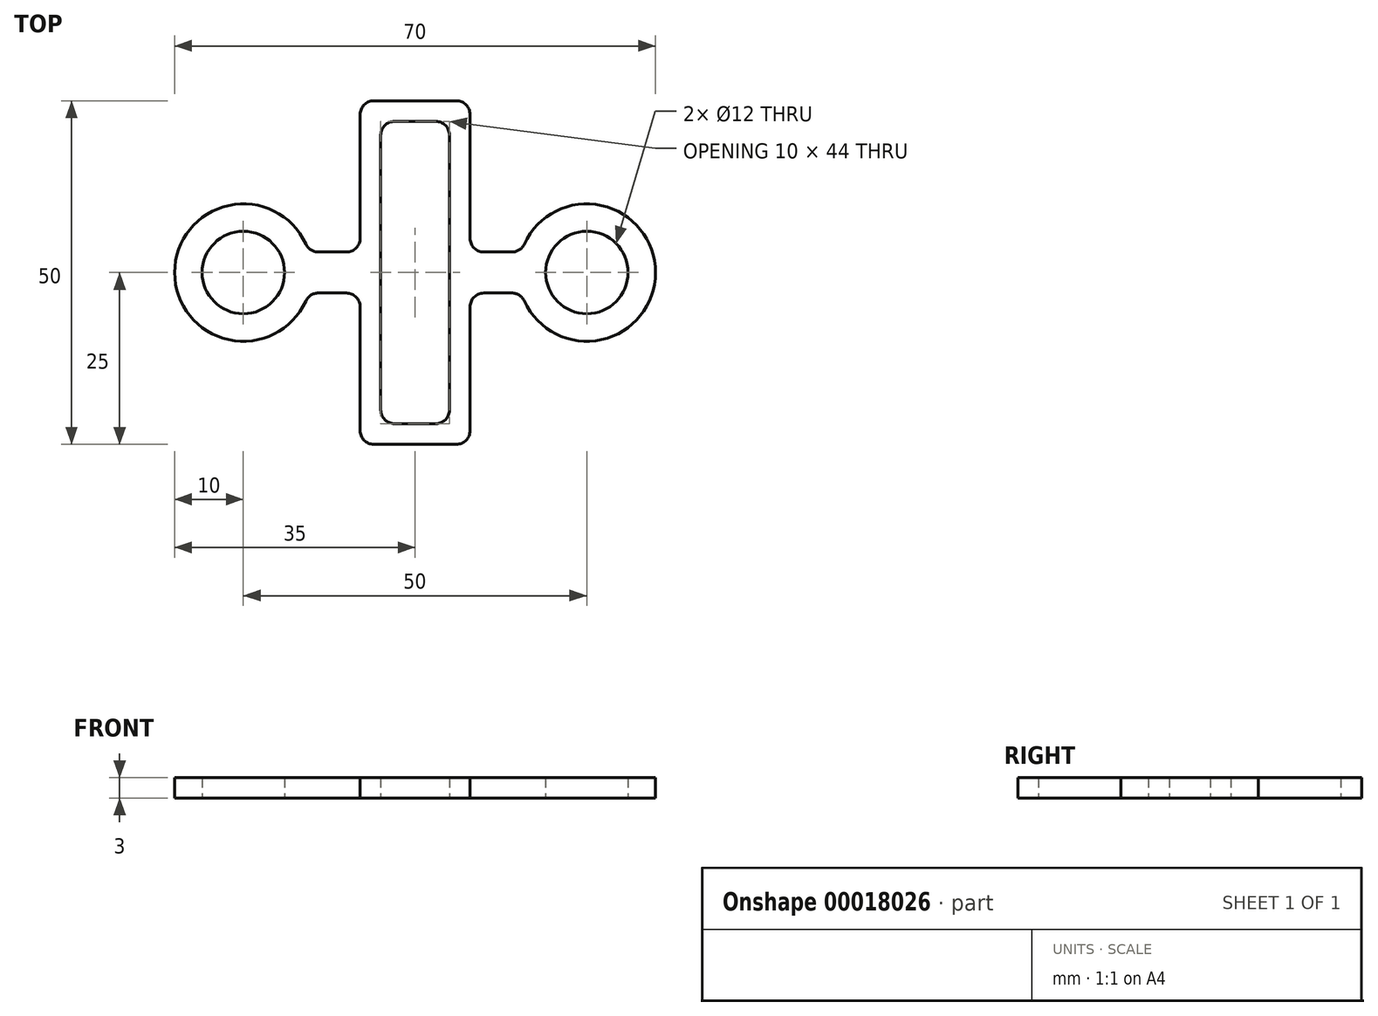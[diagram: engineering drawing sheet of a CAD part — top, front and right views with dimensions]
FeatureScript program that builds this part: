
annotation { "Feature Type Name" : "Feature", "Feature Type Description" : "" }
export const myFeature = defineFeature(function(context is Context, id is Id, definition is map)
    precondition{}
    {
        {
            var Q0;
            Q0=qCreatedBy(makeId("Top.planeOp"),FACE);
            var sketch = newSketch(context, id + "F0", { "sketchPlane" : qUnion([Q0])});
            skLineSegment(sketch, "E0", {"start": v(0, 22) * mm, "end": v(3, 22) * mm});
            skLineSegment(sketch, "E1", {"start": v(5, 20) * mm, "end": v(5, 0) * mm});
            skLineSegment(sketch, "E2", {"start": v(0, 22) * mm, "end": v(0, 25) * mm});
            skLineSegment(sketch, "E3", {"start": v(0, 25) * mm, "end": v(6, 25) * mm});
            skLineSegment(sketch, "E4", {"start": v(8, 23) * mm, "end": v(8, 4.99) * mm});
            skLineSegment(sketch, "E5", {"start": v(10, 2.99) * mm, "end": v(14.09, 2.99) * mm});
            skArc(sketch, "E6", {"start": v(35, 0) * mm, "mid": v(27.13, 9.77) * mm, "end": v(15.9, 4.16) * mm});
            skArc(sketch, "E7", {"start": v(31, 0) * mm, "mid": v(25, 6) * mm, "end": v(19, 0) * mm});
            skPoint(sketch, "E8.visualSharp", {"position": v(8, 25) * mm});
            skArc(sketch, "E8.filletArc", {"start": v(8, 23) * mm, "mid": v(7.41, 24.41) * mm, "end": v(6, 25) * mm});
            skPoint(sketch, "E9.visualSharp", {"position": v(5, 22) * mm});
            skArc(sketch, "E9.filletArc", {"start": v(5, 20) * mm, "mid": v(4.41, 21.41) * mm, "end": v(3, 22) * mm});
            skPoint(sketch, "E10.visualSharp", {"position": v(8, 2.99) * mm});
            skArc(sketch, "E10.filletArc", {"start": v(8, 4.99) * mm, "mid": v(8.59, 3.57) * mm, "end": v(10, 2.99) * mm});
            skPoint(sketch, "E11.visualSharp", {"position": v(15.46, 2.99) * mm});
            skArc(sketch, "E11.filletArc", {"start": v(14.09, 2.99) * mm, "mid": v(15.17, 3.3) * mm, "end": v(15.9, 4.16) * mm});
            skArc(sketch, "E12.MirrorCS", {"start": v(31, 0) * mm, "mid": v(25, -6) * mm, "end": v(19, 0) * mm});
            skArc(sketch, "E13.MirrorCS", {"start": v(35, 0) * mm, "mid": v(27.13, -9.77) * mm, "end": v(15.9, -4.16) * mm});
            skArc(sketch, "E14.MirrorCS", {"start": v(14.09, -2.99) * mm, "mid": v(15.17, -3.3) * mm, "end": v(15.9, -4.16) * mm});
            skLineSegment(sketch, "E15.MirrorCS", {"start": v(10, -2.99) * mm, "end": v(14.09, -2.99) * mm});
            skArc(sketch, "E16.MirrorCS", {"start": v(8, -4.99) * mm, "mid": v(8.59, -3.57) * mm, "end": v(10, -2.99) * mm});
            skLineSegment(sketch, "E17.MirrorCS", {"start": v(5, -20) * mm, "end": v(5, 0) * mm});
            skLineSegment(sketch, "E18.MirrorCS", {"start": v(0, -22) * mm, "end": v(3, -22) * mm});
            skArc(sketch, "E19.MirrorCS", {"start": v(5, -20) * mm, "mid": v(4.41, -21.41) * mm, "end": v(3, -22) * mm});
            skLineSegment(sketch, "E20.MirrorCS", {"start": v(0, -25) * mm, "end": v(6, -25) * mm});
            skLineSegment(sketch, "E21.MirrorCS", {"start": v(8, -23) * mm, "end": v(8, -4.99) * mm});
            skArc(sketch, "E22.MirrorCS", {"start": v(8, -23) * mm, "mid": v(7.41, -24.41) * mm, "end": v(6, -25) * mm});
            skArc(sketch, "E23.MirrorCS", {"start": v(-14.09, 2.99) * mm, "mid": v(-15.17, 3.3) * mm, "end": v(-15.9, 4.16) * mm});
            skArc(sketch, "E24.MirrorCS", {"start": v(-14.09, -2.99) * mm, "mid": v(-15.17, -3.3) * mm, "end": v(-15.9, -4.16) * mm});
            skArc(sketch, "E25.MirrorCS", {"start": v(-8, 4.99) * mm, "mid": v(-8.59, 3.57) * mm, "end": v(-10, 2.99) * mm});
            skArc(sketch, "E26.MirrorCS", {"start": v(-5, 20) * mm, "mid": v(-4.41, 21.41) * mm, "end": v(-3, 22) * mm});
            skArc(sketch, "E27.MirrorCS", {"start": v(-8, 23) * mm, "mid": v(-7.41, 24.41) * mm, "end": v(-6, 25) * mm});
            skArc(sketch, "E28.MirrorCS", {"start": v(-8, -4.99) * mm, "mid": v(-8.59, -3.57) * mm, "end": v(-10, -2.99) * mm});
            skLineSegment(sketch, "E29.MirrorCS", {"start": v(0, -22) * mm, "end": v(-3, -22) * mm});
            skLineSegment(sketch, "E30.MirrorCS", {"start": v(0, -25) * mm, "end": v(-6, -25) * mm});
            skArc(sketch, "E31.MirrorCS", {"start": v(-8, -23) * mm, "mid": v(-7.41, -24.41) * mm, "end": v(-6, -25) * mm});
            skArc(sketch, "E32.MirrorCS", {"start": v(-31, 0) * mm, "mid": v(-25, -6) * mm, "end": v(-19, 0) * mm});
            skArc(sketch, "E33.MirrorCS", {"start": v(-31, 0) * mm, "mid": v(-25, 6) * mm, "end": v(-19, 0) * mm});
            skArc(sketch, "E34.MirrorCS", {"start": v(-35, 0) * mm, "mid": v(-27.13, 9.77) * mm, "end": v(-15.9, 4.16) * mm});
            skPoint(sketch, "E35.MirrorP", {"position": v(-8, 25) * mm});
            skLineSegment(sketch, "E36.MirrorCS", {"start": v(-10, 2.99) * mm, "end": v(-14.09, 2.99) * mm});
            skLineSegment(sketch, "E37.MirrorCS", {"start": v(-8, 23) * mm, "end": v(-8, 4.99) * mm});
            skPoint(sketch, "E38.MirrorP", {"position": v(-5, 22) * mm});
            skLineSegment(sketch, "E39.MirrorCS", {"start": v(0, 25) * mm, "end": v(-6, 25) * mm});
            skPoint(sketch, "E40.MirrorP", {"position": v(-15.46, 2.99) * mm});
            skLineSegment(sketch, "E41.MirrorCS", {"start": v(-5, 20) * mm, "end": v(-5, 0) * mm});
            skLineSegment(sketch, "E42.MirrorCS", {"start": v(-10, -2.99) * mm, "end": v(-14.09, -2.99) * mm});
            skLineSegment(sketch, "E43.MirrorCS", {"start": v(-8, -23) * mm, "end": v(-8, -4.99) * mm});
            skLineSegment(sketch, "E44.MirrorCS", {"start": v(-5, -20) * mm, "end": v(-5, 0) * mm});
            skLineSegment(sketch, "E45.MirrorCS", {"start": v(0, 22) * mm, "end": v(-3, 22) * mm});
            skArc(sketch, "E46.MirrorCS", {"start": v(-5, -20) * mm, "mid": v(-4.41, -21.41) * mm, "end": v(-3, -22) * mm});
            skPoint(sketch, "E47.MirrorP", {"position": v(-8, 2.99) * mm});
            skArc(sketch, "E48.MirrorCS", {"start": v(-35, 0) * mm, "mid": v(-27.13, -9.77) * mm, "end": v(-15.9, -4.16) * mm});
            skSolve(sketch);
        }
        {
            var Q0;
            Q0=makeQuery(id+"F0.imprint","IMPRINT",FACE,{"disambiguationData":[TD([[makeQuery(id+"F0.imprint","IMPRINT",EDGE,{"derivedFrom":sQuery(id+"F0.wireOp",EDGE,"E0")}),1.0]])]});
            extrude(context, id + "F1", {"entities" : qUnion([Q0]), "depth" : 3 * mm});
        }
    });
